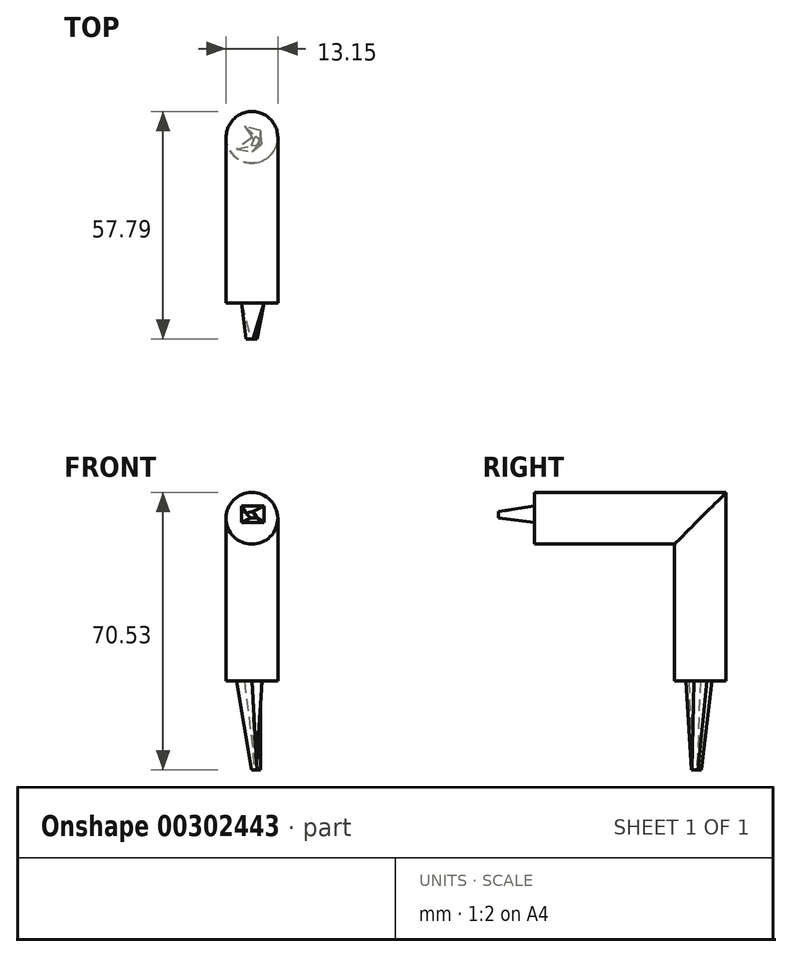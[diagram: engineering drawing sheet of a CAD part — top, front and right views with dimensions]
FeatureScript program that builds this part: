
annotation { "Feature Type Name" : "Feature", "Feature Type Description" : "" }
export const myFeature = defineFeature(function(context is Context, id is Id, definition is map)
    precondition{}
    {
        {
            var Q0;
            Q0=qCreatedBy(makeId("Front.planeOp"),FACE);
            var sketch = newSketch(context, id + "F0", { "sketchPlane" : qUnion([Q0])});
            skCircle(sketch, "E0", {"center": v(-22.96, 15.17) * mm, "radius": 6.57 * mm});
            skSolve(sketch);
        }
        {
            var Q0;
            Q0=qCreatedBy(makeId("Right.planeOp"),FACE);
            var sketch = newSketch(context, id + "F1", { "sketchPlane" : qUnion([Q0])});
            skLineSegment(sketch, "E1", {"start": v(0, 15.17) * mm, "end": v(42.08, 15.17) * mm});
            skLineSegment(sketch, "E2", {"start": v(42.08, 15.17) * mm, "end": v(42.08, -26.19) * mm});
            skSolve(sketch);
        }
        {
            var Q0;
            Q0 = qSketchRegion(id + "F0", true);
            var Q1;
            Q1 = qConstructionFilter(qBodyType(qCreatedBy(id + "F1" ,EDGE), BodyType.WIRE), ConstructionObject.NO);
            sweep(context, id + "F2", {"profiles" : qUnion([Q0]), "path" : qUnion([Q1])});
        }
        {
            var Q0;
            Q0=makeQuery(id+"F2.opSweep","CAP_FACE",FACE,{"disambiguationData":[OSD([sQuery(id+"F0.wireOp",EDGE,"E0"),sQuery(id+"F1.wireOp",VERTEX,"E1.start")])],"isStart":true});
            var sketch = newSketch(context, id + "F3", { "sketchPlane" : qUnion([Q0])});
            skLineSegment(sketch, "E3.bottom", {"start": v(-25.6, 18.27) * mm, "end": v(-19.92, 18.27) * mm});
            skLineSegment(sketch, "E3.top", {"start": v(-25.6, 14.17) * mm, "end": v(-19.92, 14.17) * mm});
            skLineSegment(sketch, "E3.left", {"start": v(-25.6, 18.27) * mm, "end": v(-25.6, 14.17) * mm});
            skLineSegment(sketch, "E3.right", {"start": v(-19.92, 18.27) * mm, "end": v(-19.92, 14.17) * mm});
            skSolve(sketch);
        }
        {
            var Q0;
            Q0=makeQuery(id+"F3.imprint","IMPRINT",FACE,{"disambiguationData":[TD([[makeQuery(id+"F3.imprint","IMPRINT",EDGE,{"derivedFrom":sQuery(id+"F3.wireOp",EDGE,"E3.bottom")}),1.0]])]});
            cPlane(context, id + "F4", {"entities" : qUnion([Q0]), "cplaneType" : CPlaneType.OFFSET, "offset" : 9.14 * mm, "width" : 152.4 * mm, "height" : 152.4 * mm});
        }
        {
            var Q0;
            Q0=qCreatedBy(id+"F4.planeOp",FACE);
            var sketch = newSketch(context, id + "F5", { "sketchPlane" : qUnion([Q0])});
            skLineSegment(sketch, "E4", {"start": v(-23.3, 15.31) * mm, "end": v(-21.64, 15.31) * mm});
            skLineSegment(sketch, "E5", {"start": v(-21.64, 15.31) * mm, "end": v(-22.68, 16.87) * mm});
            skLineSegment(sketch, "E6", {"start": v(-22.68, 16.87) * mm, "end": v(-24.43, 16.5) * mm});
            skLineSegment(sketch, "E7", {"start": v(-24.43, 16.5) * mm, "end": v(-23.3, 15.31) * mm});
            skSolve(sketch);
        }
        {
            var Q1;
            Q1=makeQuery(id+"F3.imprint","IMPRINT",FACE,{"disambiguationData":[TD([[makeQuery(id+"F3.imprint","IMPRINT",EDGE,{"derivedFrom":sQuery(id+"F3.wireOp",EDGE,"E3.bottom")}),-1.0]])]});
            var Q2;
            Q2=makeQuery(id+"F5.imprint","IMPRINT",FACE,{"disambiguationData":[TD([[makeQuery(id+"F5.imprint","IMPRINT",EDGE,{"derivedFrom":sQuery(id+"F5.wireOp",EDGE,"E4")}),1.0]])]});
            loft(context, id + "F6", {"operationType" : NewBodyOperationType.ADD, "sheetProfilesArray" : [{ "sheetProfileEntities" : qUnion([Q1]) }, { "sheetProfileEntities" : qUnion([Q2]) }]});
        }
        {
            var Q0;
            Q0=makeQuery(id+"F2.opSweep","CAP_FACE",FACE,{"disambiguationData":[OSD([sQuery(id+"F0.wireOp",EDGE,"E0"),sQuery(id+"F1.wireOp",VERTEX,"E2.end")])],"isStart":false});
            var sketch = newSketch(context, id + "F7", { "sketchPlane" : qUnion([Q0])});
            skLineSegment(sketch, "E8", {"start": v(-26.9, -39.17) * mm, "end": v(-22.9, -38.47) * mm});
            skLineSegment(sketch, "E9", {"start": v(-22.9, -38.47) * mm, "end": v(-20.39, -40.52) * mm});
            skLineSegment(sketch, "E10", {"start": v(-20.39, -40.52) * mm, "end": v(-20.77, -43.8) * mm});
            skLineSegment(sketch, "E11", {"start": v(-20.77, -43.8) * mm, "end": v(-24.9, -44.99) * mm});
            skLineSegment(sketch, "E12", {"start": v(-24.9, -44.99) * mm, "end": v(-22.96, -42.08) * mm});
            skLineSegment(sketch, "E13", {"start": v(-22.96, -42.08) * mm, "end": v(-26.9, -39.17) * mm});
            skSolve(sketch);
        }
        {
            var Q0;
            Q0=makeQuery(id+"F7.imprint","IMPRINT",FACE,{"disambiguationData":[TD([[makeQuery(id+"F7.imprint","IMPRINT",EDGE,{"derivedFrom":sQuery(id+"F7.wireOp",EDGE,"E8")}),1.0]])]});
            cPlane(context, id + "F8", {"entities" : qUnion([Q0]), "cplaneType" : CPlaneType.OFFSET, "offset" : 22.6 * mm, "width" : 152.4 * mm, "height" : 152.4 * mm});
        }
        {
            var Q0;
            Q0=qCreatedBy(id+"F8.planeOp",FACE);
            var sketch = newSketch(context, id + "F9", { "sketchPlane" : qUnion([Q0])});
            skLineSegment(sketch, "E14", {"start": v(-23, -40) * mm, "end": v(-22.08, -42.42) * mm});
            skLineSegment(sketch, "E15", {"start": v(-22.08, -42.42) * mm, "end": v(-20.78, -41.44) * mm});
            skLineSegment(sketch, "E16", {"start": v(-20.78, -41.44) * mm, "end": v(-21.88, -39.98) * mm});
            skLineSegment(sketch, "E17", {"start": v(-21.66, -39.82) * mm, "end": v(-23, -40) * mm});
            skLineSegment(sketch, "E18", {"start": v(-21.66, -39.82) * mm, "end": v(-21.88, -39.98) * mm});
            skSolve(sketch);
        }
        {
            var Q1;
            Q1=makeQuery(id+"F7.imprint","IMPRINT",FACE,{"disambiguationData":[TD([[makeQuery(id+"F7.imprint","IMPRINT",EDGE,{"derivedFrom":sQuery(id+"F7.wireOp",EDGE,"E8")}),-1.0]])]});
            var Q2;
            Q2=makeQuery(id+"F9.imprint","IMPRINT",FACE,{"disambiguationData":[TD([[makeQuery(id+"F9.imprint","IMPRINT",EDGE,{"derivedFrom":sQuery(id+"F9.wireOp",EDGE,"E14")}),1.0]])]});
            loft(context, id + "F10", {"operationType" : NewBodyOperationType.ADD, "sheetProfilesArray" : [{ "sheetProfileEntities" : qUnion([Q1]) }, { "sheetProfileEntities" : qUnion([Q2]) }]});
        }
    });
